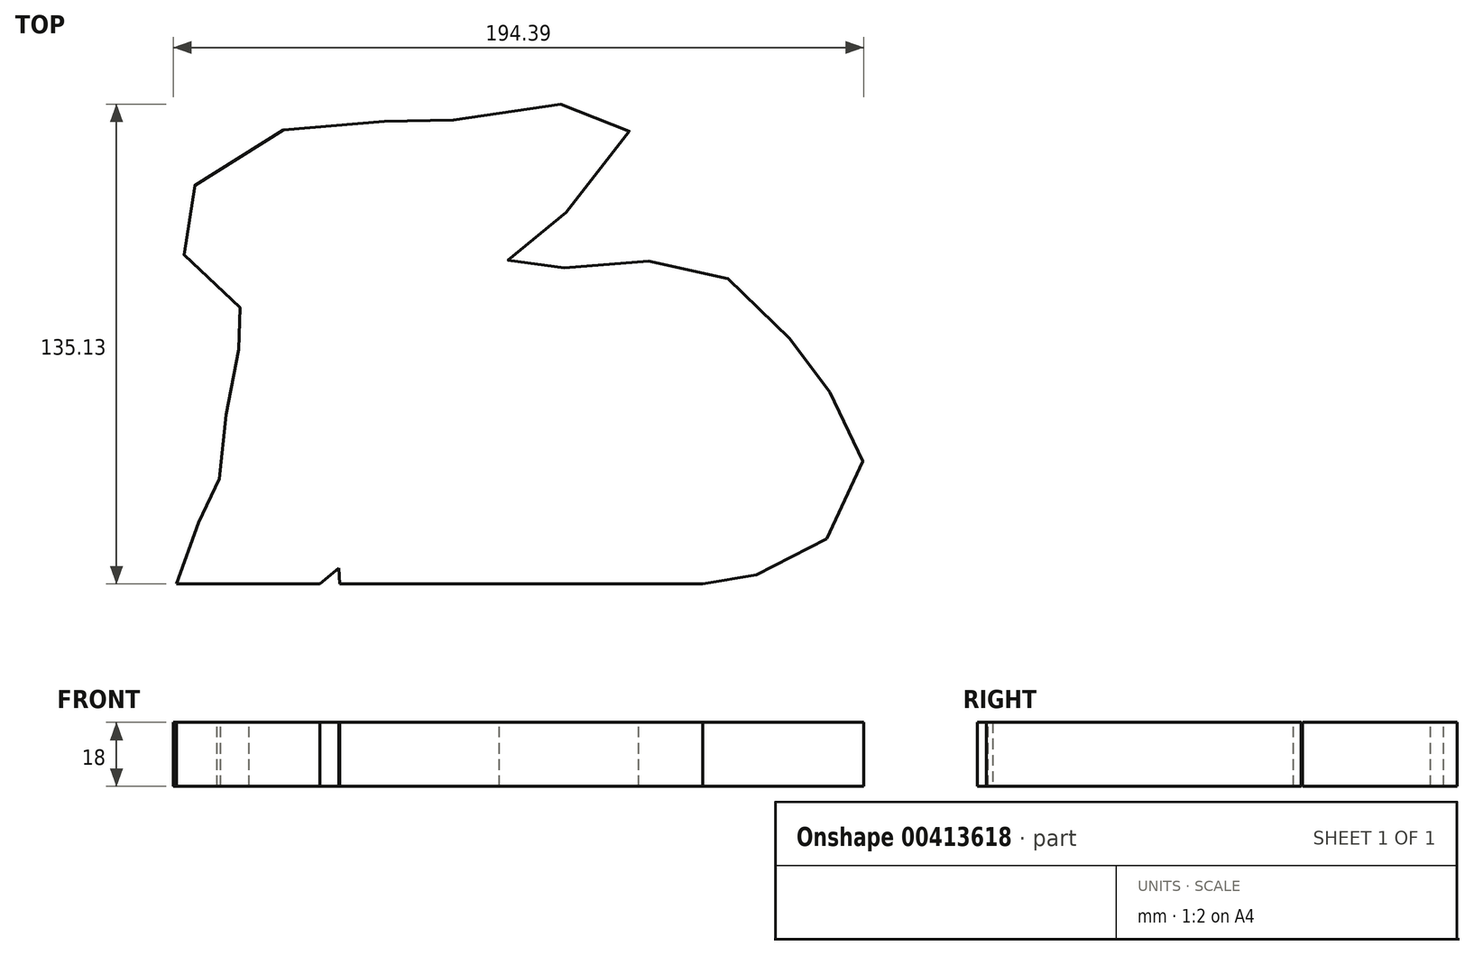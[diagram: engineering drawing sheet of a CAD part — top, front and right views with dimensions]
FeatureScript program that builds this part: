
annotation { "Feature Type Name" : "Feature", "Feature Type Description" : "" }
export const myFeature = defineFeature(function(context is Context, id is Id, definition is map)
    precondition{}
    {
        {
            var Q0;
            Q0=qCreatedBy(makeId("Top.planeOp"),FACE);
            var sketch = newSketch(context, id + "F0", { "sketchPlane" : qUnion([Q0])});
            skFitSpline(sketch, "E0", {"points": [v(3.96, 1.07) * mm, v(4.22, 6.64) * mm, v(5.68, 12.68) * mm, v(12.32, 20.57) * mm, v(15.5, 23.76) * mm, v(16.3, 25.22) * mm, v(16.23, 28.2) * mm, v(15.37, 37.7) * mm, v(16.43, 44.92) * mm, v(17.7, 47.71) * mm, v(18.12, 54.85) * mm, v(19.11, 61.45) * mm, v(21.97, 68.18) * mm, v(23.77, 71.76) * mm, v(24.36, 73.54) * mm, v(22.78, 77.02) * mm, v(21.2, 79.74) * mm, v(12.71, 86.98) * mm, v(6.3, 93.4) * mm, v(3.9, 96.63) * mm, v(3.84, 105.4) * mm, v(16.52, 119.9) * mm, v(30.6, 127.59) * mm, v(46.92, 132) * mm, v(63.06, 131.15) * mm, v(70.66, 128.71) * mm, v(76.3, 129.84) * mm, v(91.86, 134.16) * mm, v(110.87, 136.11) * mm, v(122.53, 134.38) * mm, v(129.45, 130.53) * mm, v(133.13, 126.18) * mm, v(132.68, 120.04) * mm, v(95.52, 94.86) * mm, v(94.82, 94.22) * mm, v(95.3, 93.22) * mm, v(96.73, 92.21) * mm, v(102.5, 92.64) * mm, v(108.57, 91.49) * mm, v(110.79, 90.24) * mm, v(122.37, 91.2) * mm, v(131.52, 92.22) * mm, v(144.19, 91.14) * mm, v(152.25, 89.73) * mm, v(164.17, 84.2) * mm, v(172.8, 76.08) * mm, v(177.93, 66.82) * mm, v(180.6, 59) * mm, v(187.08, 55.55) * mm, v(193.22, 49.75) * mm, v(197.35, 41.15) * mm, v(195.12, 25.75) * mm, v(191.88, 18.39) * mm, v(178.49, 7.23) * mm, v(171.92, 3.87) * mm, v(165.4, 3.64) * mm, v(160.02, 4.09) * mm, v(157.56, 3.69) * mm, v(152.19, 0.99) * mm, v(152.19, 1.06) * mm], "startDerivative": vector(14.36, 384.07) * mm, "endDerivative": vector(22.2, 56.9) * mm});
            skLineSegment(sketch, "E1", {"start": v(3.96, 1.07) * mm, "end": v(44.34, 1.07) * mm});
            skLineSegment(sketch, "E2", {"start": v(44.34, 1.07) * mm, "end": v(49.7, 5.4) * mm});
            skLineSegment(sketch, "E3", {"start": v(49.7, 5.4) * mm, "end": v(49.94, 1.05) * mm});
            skLineSegment(sketch, "E4", {"start": v(49.94, 1.05) * mm, "end": v(152.19, 0.99) * mm});
            skSolve(sketch);
        }
        {
            var Q0;
            {var subQ0=sQuery(id+"F0.wireOp",EDGE,"E1");Q0=makeQuery(id+"F0.imprint","IMPRINT",FACE,{"disambiguationData":[TD([[makeQuery(id+"F0.imprint","IMPRINT",EDGE,{"derivedFrom":subQ0}),1.0]])]});}
            extrude(context, id + "F1", {"entities" : qUnion([Q0]), "depth" : 18 * mm});
        }
    });
